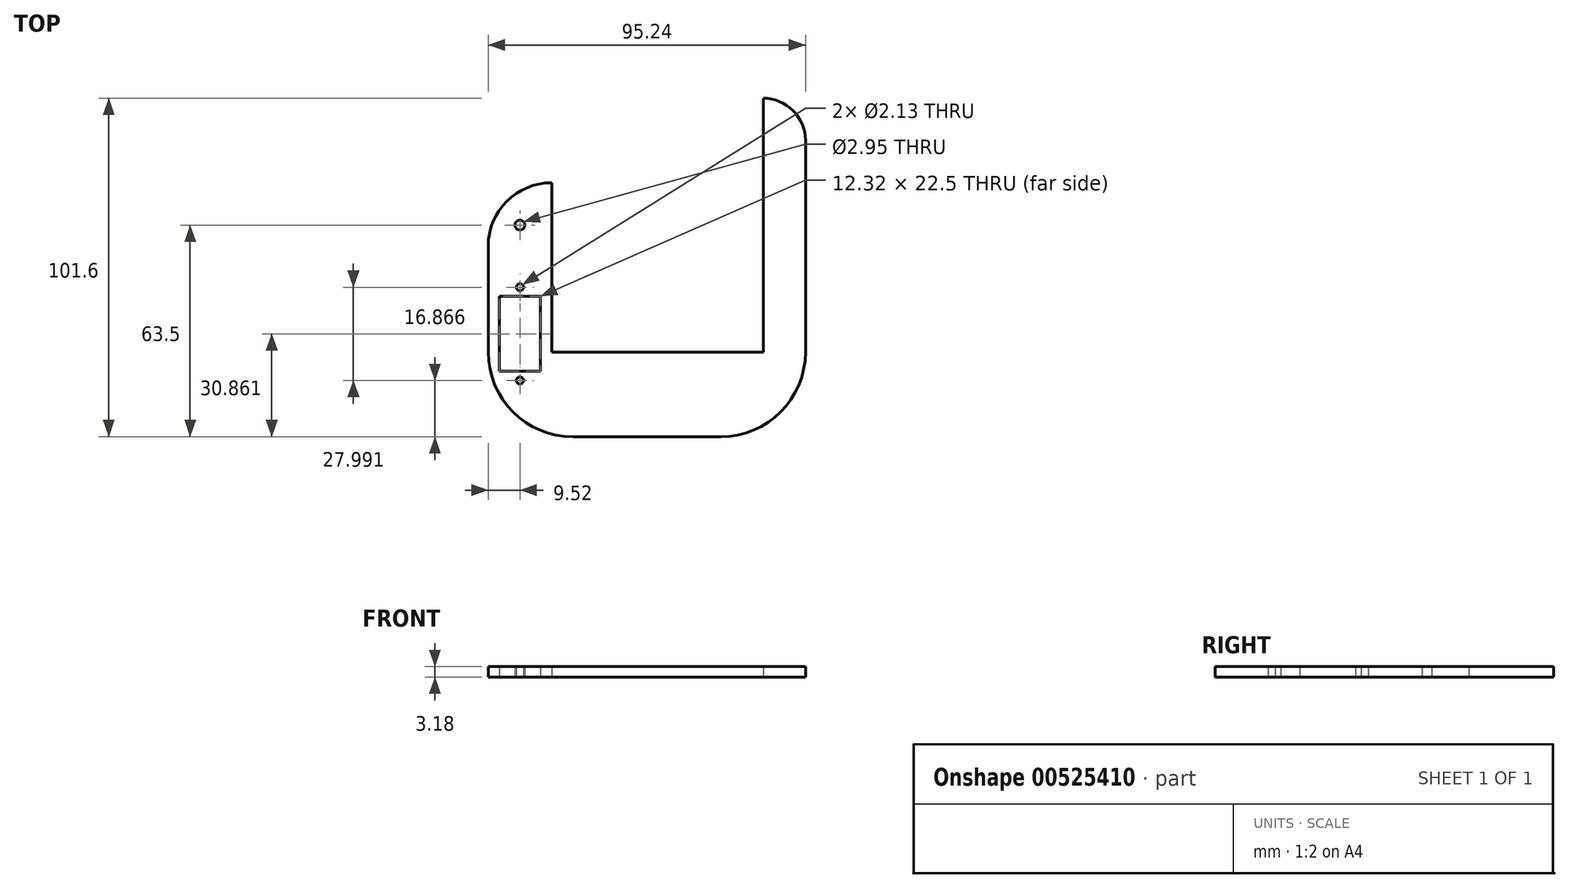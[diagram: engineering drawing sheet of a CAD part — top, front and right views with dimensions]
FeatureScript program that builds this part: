
annotation { "Feature Type Name" : "Feature", "Feature Type Description" : "" }
export const myFeature = defineFeature(function(context is Context, id is Id, definition is map)
    precondition{}
    {
        {
            var Q0;
            Q0=qCreatedBy(makeId("Top.planeOp"),FACE);
            var sketch = newSketch(context, id + "F0", { "sketchPlane" : qUnion([Q0])});
            skLineSegment(sketch, "E0.bottom", {"start": v(34.93, 12.7) * mm, "end": v(-28.57, 12.7) * mm});
            skLineSegment(sketch, "E0.top", {"start": v(22.23, -12.7) * mm, "end": v(-22.23, -12.7) * mm});
            skLineSegment(sketch, "E0.left", {"start": v(47.63, 12.7) * mm, "end": v(47.63, 12.7) * mm});
            skLineSegment(sketch, "E0.right", {"start": v(-47.63, 12.7) * mm, "end": v(-47.63, 12.7) * mm});
            skPoint(sketch, "E0.middle", {"position": v(0, 0) * mm});
            skLineSegment(sketch, "E1.top", {"start": v(-28.58, 63.5) * mm, "end": v(-28.58, 63.5) * mm});
            skLineSegment(sketch, "E1.left", {"start": v(-47.62, 12.7) * mm, "end": v(-47.63, 44.45) * mm});
            skLineSegment(sketch, "E1.right", {"start": v(-28.57, 12.7) * mm, "end": v(-28.58, 63.5) * mm});
            skLineSegment(sketch, "E2.top", {"start": v(41.02, 88.9) * mm, "end": v(34.92, 88.9) * mm});
            skLineSegment(sketch, "E2.left", {"start": v(47.63, 12.7) * mm, "end": v(47.62, 76.2) * mm});
            skLineSegment(sketch, "E2.right", {"start": v(34.93, 12.7) * mm, "end": v(34.92, 82.8) * mm});
            skCircle(sketch, "E3", {"center": v(-38.1, 12.7) * mm, "radius": 1.52 * mm, "construction": true});
            skCircle(sketch, "E4", {"center": v(-38.1, 50.8) * mm, "radius": 1.47 * mm});
            skLineSegment(sketch, "E5", {"start": v(-28.57, 12.7) * mm, "end": v(-38.1, 12.7) * mm, "construction": true});
            skLineSegment(sketch, "E6", {"start": v(-38.1, 12.7) * mm, "end": v(-47.63, 12.7) * mm, "construction": true});
            skLineSegment(sketch, "E7.bottom", {"start": v(-31.94, 29.41) * mm, "end": v(-44.26, 29.41) * mm});
            skLineSegment(sketch, "E7.top", {"start": v(-31.94, 6.9) * mm, "end": v(-44.26, 6.9) * mm});
            skLineSegment(sketch, "E7.left", {"start": v(-31.94, 29.41) * mm, "end": v(-31.94, 6.9) * mm});
            skLineSegment(sketch, "E7.right", {"start": v(-44.26, 29.41) * mm, "end": v(-44.26, 6.9) * mm});
            skPoint(sketch, "E7.middle", {"position": v(-38.1, 18.16) * mm});
            skCircle(sketch, "E8", {"center": v(-38.1, 4.17) * mm, "radius": 1.07 * mm});
            skPoint(sketch, "E8.centerSnap0", {"position": v(-38.1, 6.9) * mm});
            skCircle(sketch, "E9", {"center": v(-38.1, 32.16) * mm, "radius": 1.07 * mm});
            skPoint(sketch, "E9.centerSnap0", {"position": v(-38.1, 29.41) * mm});
            skPoint(sketch, "E10.visualSharp", {"position": v(-47.63, -12.7) * mm});
            skArc(sketch, "E10.filletArc", {"start": v(-47.63, 12.7) * mm, "mid": v(-40.19, -5.26) * mm, "end": v(-22.23, -12.7) * mm});
            skPoint(sketch, "E11.visualSharp", {"position": v(47.63, -12.7) * mm});
            skArc(sketch, "E11.filletArc", {"start": v(22.23, -12.7) * mm, "mid": v(40.19, -5.26) * mm, "end": v(47.63, 12.7) * mm});
            skPoint(sketch, "E12.visualSharp", {"position": v(47.62, 88.9) * mm});
            skArc(sketch, "E12.filletArc", {"start": v(47.62, 76.2) * mm, "mid": v(43.9, 85.18) * mm, "end": v(34.92, 88.9) * mm});
            skPoint(sketch, "E13.visualSharp", {"position": v(-47.63, 63.5) * mm});
            skArc(sketch, "E13.filletArc", {"start": v(-28.58, 63.5) * mm, "mid": v(-42.05, 57.92) * mm, "end": v(-47.63, 44.45) * mm});
            skLineSegment(sketch, "E14", {"start": v(34.92, 82.8) * mm, "end": v(34.92, 88.9) * mm});
            skLineSegment(sketch, "E15", {"start": v(34.92, 88.9) * mm, "end": v(34.92, 88.9) * mm});
            skSolve(sketch);
        }
        {
            var Q0;
            Q0=makeQuery(id+"F0.imprint","IMPRINT",FACE,{"disambiguationData":[TD([[makeQuery(id+"F0.imprint","IMPRINT",EDGE,{"derivedFrom":sQuery(id+"F0.wireOp",EDGE,"E0.bottom")}),1.0]])]});
            extrude(context, id + "F1", {"entities" : qUnion([Q0]), "depth" : 3.17 * mm, "offsetDistance" : 25.4 * mm});
        }
    });
